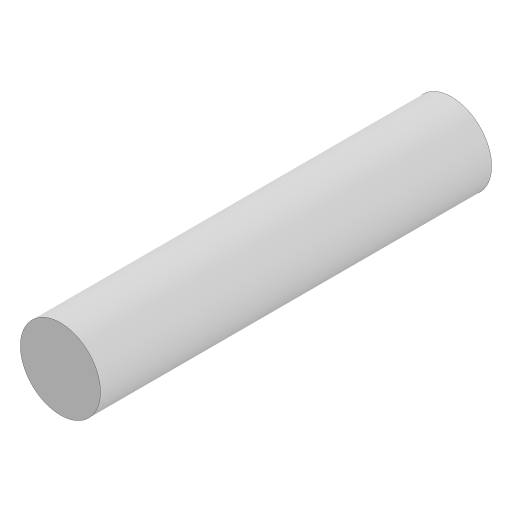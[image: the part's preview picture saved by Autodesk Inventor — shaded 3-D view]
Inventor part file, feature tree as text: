
AUTODESK INVENTOR PART (.ipt)
format: ipt  version: 2023 (Build 270158000, 158)  size: 87,040 bytes
history: native  units: mm
features: extrude x1, sketch x1
ambient origin geometry x8: Origin, YZ Plane, XZ Plane, XY Plane, X Axis, Y Axis, Z Axis, Center Point
bodies: Solid1 (feature_tree)
feature tree (2):
  extrude  "Extrusion1"  Depth=21.0mm TaperAngle=0.0deg
  sketch  "Sketch1"  dims[d0=4.3mm d1=21.0mm d2=0.0mm]
